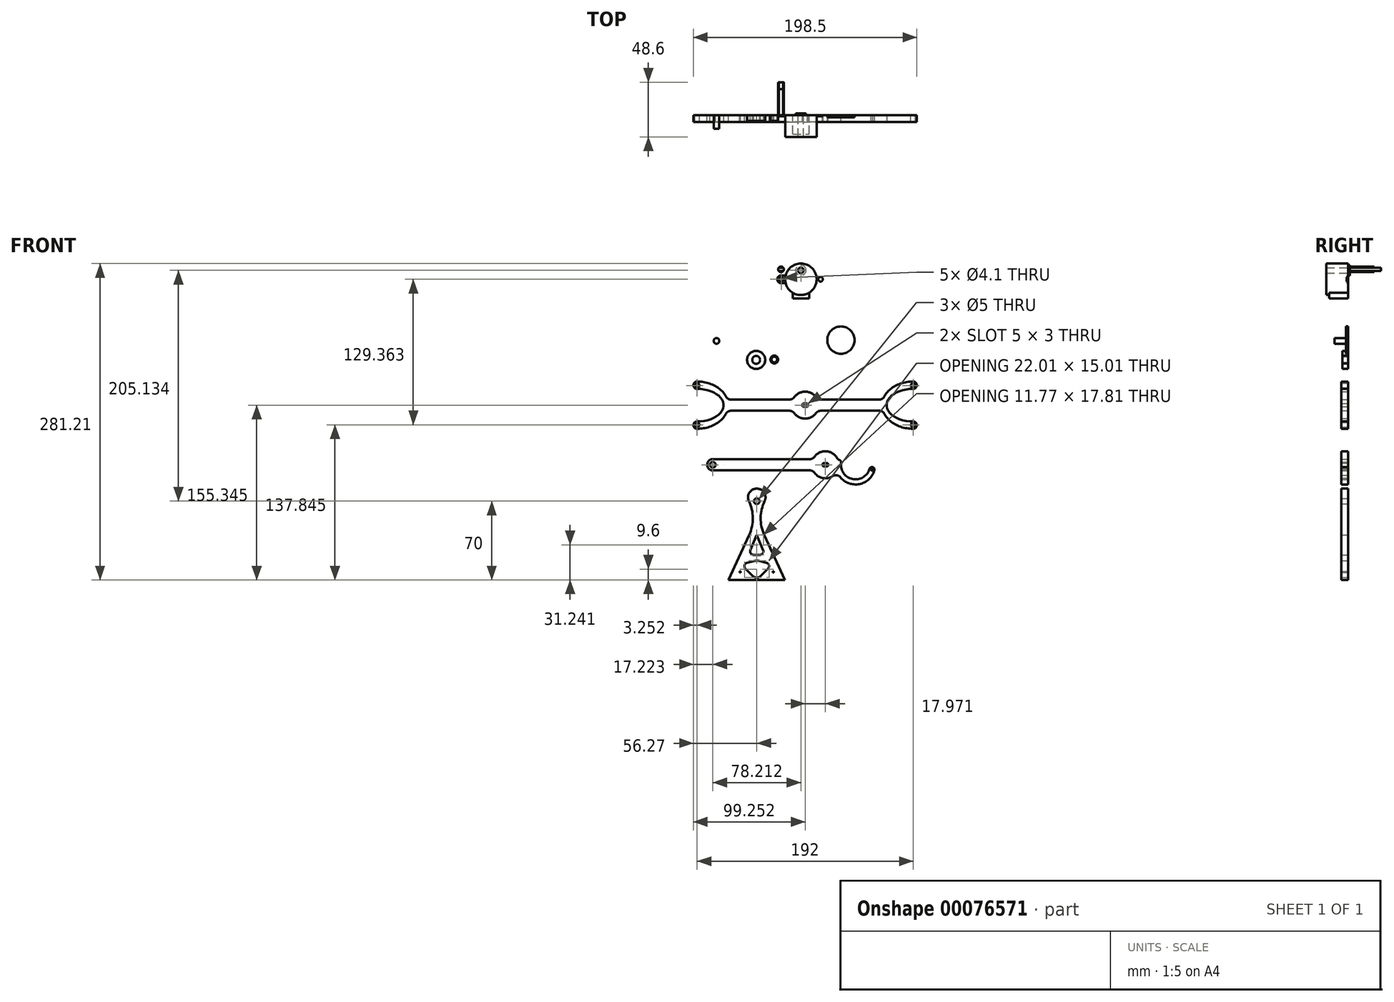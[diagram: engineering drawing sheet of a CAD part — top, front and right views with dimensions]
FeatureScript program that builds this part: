
annotation { "Feature Type Name" : "Feature", "Feature Type Description" : "" }
export const myFeature = defineFeature(function(context is Context, id is Id, definition is map)
    precondition{}
    {
        {
            var Q0;
            Q0=qCreatedBy(makeId("Front.planeOp"),FACE);
            var sketch = newSketch(context, id + "F0", { "sketchPlane" : qUnion([Q0])});
            skCircle(sketch, "E0", {"center": v(49.8, 38.16) * mm, "radius": 12.13 * mm});
            skSolve(sketch);
        }
        {
            var Q0;
            Q0=makeQuery(id+"F0.imprint","IMPRINT",FACE,{"disambiguationData":[TD([[makeQuery(id+"F0.imprint","IMPRINT",EDGE,{"derivedFrom":sQuery(id+"F0.wireOp",EDGE,"E0")}),1.0]])]});
            extrude(context, id + "F1", {"entities" : qUnion([Q0]), "depth" : 1.75 * mm});
        }
        {
            var Q0;
            Q0=qCreatedBy(makeId("Front.planeOp"),FACE);
            var sketch = newSketch(context, id + "F2", { "sketchPlane" : qUnion([Q0])});
            skLineSegment(sketch, "E1", {"start": v(-48, -14.65) * mm, "end": v(4.23, -14.65) * mm});
            skLineSegment(sketch, "E2", {"start": v(4.23, -24.65) * mm, "end": v(-48, -24.65) * mm});
            skArc(sketch, "E3", {"start": v(15.98, -18.15) * mm, "mid": v(15.48, -19.65) * mm, "end": v(15.98, -21.15) * mm});
            skArc(sketch, "E4", {"start": v(8.28, -26.71) * mm, "mid": v(12.54, -30.35) * mm, "end": v(17.98, -31.65) * mm});
            skArc(sketch, "E5.trimOffspring", {"start": v(17.98, -7.65) * mm, "mid": v(12.54, -8.96) * mm, "end": v(8.28, -12.6) * mm});
            skPoint(sketch, "E6.visualSharp", {"position": v(7.07, -14.65) * mm});
            skArc(sketch, "E6.filletArc", {"start": v(4.23, -14.65) * mm, "mid": v(6.5, -14.11) * mm, "end": v(8.28, -12.6) * mm});
            skPoint(sketch, "E7.visualSharp", {"position": v(7.07, -24.65) * mm});
            skArc(sketch, "E7.filletArc", {"start": v(8.28, -26.71) * mm, "mid": v(6.5, -25.2) * mm, "end": v(4.23, -24.65) * mm});
            skLineSegment(sketch, "E8.bottom", {"start": v(15.98, -21.15) * mm, "end": v(17.98, -21.15) * mm});
            skLineSegment(sketch, "E8.top", {"start": v(15.98, -18.15) * mm, "end": v(17.98, -18.15) * mm});
            skCircle(sketch, "E9", {"center": v(-78.02, -37.15) * mm, "radius": 2.05 * mm});
            skCircle(sketch, "E10", {"center": v(-78.02, -2.15) * mm, "radius": 2.05 * mm});
            skLineSegment(sketch, "E11", {"start": v(-78.02, -2.15) * mm, "end": v(-78.02, -37.15) * mm, "construction": true});
            skPoint(sketch, "E12", {"position": v(-78.02, -19.65) * mm});
            skEllipticalArc(sketch, "E13", {});
            skEllipticalArc(sketch, "E14", {});
            skPoint(sketch, "E15", {"position": v(-78.02, 1.35) * mm});
            skPoint(sketch, "E16", {"position": v(-78.02, -5.15) * mm});
            skPoint(sketch, "E17", {"position": v(-78.02, -40.65) * mm});
            skPoint(sketch, "E18", {"position": v(-78.02, -34.15) * mm});
            skArc(sketch, "E19", {"start": v(-78.02, 1.35) * mm, "mid": v(-81.27, -1.9) * mm, "end": v(-78.02, -5.15) * mm});
            skArc(sketch, "E20", {"start": v(-78.02, -34.15) * mm, "mid": v(-81.27, -37.4) * mm, "end": v(-78.02, -40.65) * mm});
            skEllipticalArc(sketch, "E21.trimOffspring", {});
            skPoint(sketch, "E22.visualSharp", {"position": v(-51.3, -14.65) * mm});
            skArc(sketch, "E22.filletArc", {"start": v(-52.44, -11.95) * mm, "mid": v(-50.6, -13.93) * mm, "end": v(-48, -14.65) * mm});
            skPoint(sketch, "E23.visualSharp", {"position": v(-51.3, -24.65) * mm});
            skArc(sketch, "E23.filletArc", {"start": v(-48, -24.65) * mm, "mid": v(-50.6, -25.38) * mm, "end": v(-52.44, -27.36) * mm});
            skLineSegment(sketch, "E24", {"start": v(17.98, -19.65) * mm, "end": v(17.98, 0) * mm});
            skLineSegment(sketch, "E25", {"start": v(17.98, -19.65) * mm, "end": v(17.98, -40.2) * mm});
            skPoint(sketch, "E25.endSnap0", {"position": v(17.98, -21.15) * mm});
            skArc(sketch, "E26.MirrorCS", {"start": v(27.69, -26.71) * mm, "mid": v(23.43, -30.35) * mm, "end": v(17.98, -31.65) * mm});
            skArc(sketch, "E27.MirrorCS", {"start": v(17.98, -7.65) * mm, "mid": v(23.43, -8.96) * mm, "end": v(27.69, -12.6) * mm});
            skArc(sketch, "E28.MirrorCS", {"start": v(31.73, -14.65) * mm, "mid": v(29.46, -14.11) * mm, "end": v(27.69, -12.6) * mm});
            skLineSegment(sketch, "E29.MirrorCS", {"start": v(19.98, -18.15) * mm, "end": v(17.98, -18.15) * mm});
            skArc(sketch, "E30.MirrorCS", {"start": v(19.98, -18.15) * mm, "mid": v(20.48, -19.65) * mm, "end": v(19.98, -21.15) * mm});
            skLineSegment(sketch, "E31.MirrorCS", {"start": v(19.98, -21.15) * mm, "end": v(17.98, -21.15) * mm});
            skArc(sketch, "E32.MirrorCS", {"start": v(27.69, -26.71) * mm, "mid": v(29.46, -25.2) * mm, "end": v(31.73, -24.65) * mm});
            skLineSegment(sketch, "E33.MirrorCS", {"start": v(83.96, -14.65) * mm, "end": v(31.73, -14.65) * mm});
            skLineSegment(sketch, "E34.MirrorCS", {"start": v(31.73, -24.65) * mm, "end": v(83.96, -24.65) * mm});
            skArc(sketch, "E35.MirrorCS", {"start": v(83.96, -24.65) * mm, "mid": v(86.56, -25.38) * mm, "end": v(88.4, -27.36) * mm});
            skArc(sketch, "E36.MirrorCS", {"start": v(88.4, -11.95) * mm, "mid": v(86.56, -13.93) * mm, "end": v(83.96, -14.65) * mm});
            skEllipticalArc(sketch, "E37.MirrorCS", {});
            skArc(sketch, "E38.MirrorCS", {"start": v(113.98, 1.35) * mm, "mid": v(117.23, -1.9) * mm, "end": v(113.98, -5.15) * mm});
            skCircle(sketch, "E39.MirrorC", {"center": v(113.98, -2.15) * mm, "radius": 2.05 * mm});
            skEllipticalArc(sketch, "E40.MirrorCS", {});
            skArc(sketch, "E41.MirrorCS", {"start": v(113.98, -34.15) * mm, "mid": v(117.23, -37.4) * mm, "end": v(113.98, -40.65) * mm});
            skCircle(sketch, "E42.MirrorC", {"center": v(113.98, -37.15) * mm, "radius": 2.05 * mm});
            skEllipticalArc(sketch, "E43.MirrorCS", {});
            const initialGuessF2  = {"E13": [-0.07801780587148666, -0.01965486932093423, 0, -1, 0.021, 0.0275, 6.283185307179586, 1.1950960830232749], "E14": [-0.07801780587148666, -0.01965486932093423, -1, 0, 0.0235, 0.0145, 1.5707963267948966, 4.71238898038469], "E21.trimOffspring": [-0.07801780587148666, -0.01965486932093423, 0, -1, 0.021, 0.0275, 1.9464965705665191, 3.141592653589793], "E37.MirrorCS": [0.11398219412851335, -0.01965486932093423, 0, -1, 0.021, 0.0275, 3.141592653589793, 4.336688736613067], "E40.MirrorCS": [0.11398219412851335, -0.01965486932093423, 1, 0, 0.0235, 0.0145, 1.5707963267948966, 4.71238898038469], "E43.MirrorCS": [0.11398219412851335, -0.01965486932093423, 0, -1, 0.021, 0.0275, 5.088089224156311, 6.283185307179586]};
            skSetInitialGuess(sketch, initialGuessF2);
            skSolve(sketch);
        }
        {
            var Q0;
            Q0 = qSketchRegion(id + "F2", true);
            extrude(context, id + "F3", {"entities" : qUnion([Q0]), "depth" : 6 * mm});
        }
        {
            var Q0;
            Q0=qCreatedBy(makeId("Front.planeOp"),FACE);
            var sketch = newSketch(context, id + "F4", { "sketchPlane" : qUnion([Q0])});
            skCircle(sketch, "E44", {"center": v(-60.76, 37.44) * mm, "radius": 2.5 * mm});
            skSolve(sketch);
        }
        {
            var Q0;
            Q0 = qSketchRegion(id + "F4", true);
            extrude(context, id + "F5", {"entities" : qUnion([Q0]), "depth" : 12 * mm});
        }
        {
            var Q0;
            Q0=qCreatedBy(makeId("Front.planeOp"),FACE);
            var sketch = newSketch(context, id + "F6", { "sketchPlane" : qUnion([Q0])});
            skCircle(sketch, "E45", {"center": v(-25.53, 20.6) * mm, "radius": 3.5 * mm});
            skCircle(sketch, "E46", {"center": v(-25.53, 20.6) * mm, "radius": 8 * mm});
            skSolve(sketch);
        }
        {
            var Q0;
            Q0=makeQuery(id+"F6.imprint","IMPRINT",FACE,{"disambiguationData":[TD([[makeQuery(id+"F6.imprint","IMPRINT",EDGE,{"derivedFrom":sQuery(id+"F6.wireOp",EDGE,"E45")}),-1.0]])]});
            extrude(context, id + "F7", {"entities" : qUnion([Q0]), "depth" : 5 * mm});
        }
        {
            var Q0;
            Q0=qCreatedBy(makeId("Front.planeOp"),FACE);
            var sketch = newSketch(context, id + "F8", { "sketchPlane" : qUnion([Q0])});
            skCircle(sketch, "E47", {"center": v(-9.4, 20.94) * mm, "radius": 3.5 * mm});
            skCircle(sketch, "E48", {"center": v(-9.4, 20.94) * mm, "radius": 2.5 * mm});
            skSolve(sketch);
        }
        {
            var Q0;
            Q0=makeQuery(id+"F8.imprint","IMPRINT",FACE,{"disambiguationData":[TD([[makeQuery(id+"F8.imprint","IMPRINT",EDGE,{"derivedFrom":sQuery(id+"F8.wireOp",EDGE,"E47")}),1.0]])]});
            extrude(context, id + "F9", {"entities" : qUnion([Q0]), "depth" : 5 * mm});
        }
        {
            var Q0;
            Q0=qCreatedBy(makeId("Front.planeOp"),FACE);
            var sketch = newSketch(context, id + "F10", { "sketchPlane" : qUnion([Q0])});
            skCircle(sketch, "E49", {"center": v(-25, -105) * mm, "radius": 2.5 * mm});
            skLineSegment(sketch, "E50", {"start": v(-50, -175) * mm, "end": v(0, -175) * mm});
            skLineSegment(sketch, "E51", {"start": v(-25, -175) * mm, "end": v(-25, -70.8) * mm, "construction": true});
            skLineSegment(sketch, "E52", {"start": v(-32, -105) * mm, "end": v(0, -175) * mm, "construction": true});
            skLineSegment(sketch, "E53", {"start": v(-18, -105) * mm, "end": v(-50, -175) * mm, "construction": true});
            skPoint(sketch, "E54.visualSharp", {"position": v(-50, -175) * mm});
            skPoint(sketch, "E55.visualSharp", {"position": v(0, -175) * mm});
            skLineSegment(sketch, "E56", {"start": v(-31.65, -134.85) * mm, "end": v(-50, -175) * mm});
            skLineSegment(sketch, "E57", {"start": v(0, -175) * mm, "end": v(-18.35, -134.85) * mm});
            skPoint(sketch, "E58.visualSharp", {"position": v(-25, -120.31) * mm});
            skArc(sketch, "E58.filletArc", {"start": v(-31.65, -134.85) * mm, "mid": v(-28.48, -119.89) * mm, "end": v(-32, -105) * mm});
            skArc(sketch, "E59.filletArc", {"start": v(-18, -105) * mm, "mid": v(-21.52, -119.89) * mm, "end": v(-18.35, -134.85) * mm});
            skPoint(sketch, "E60.visualSharp", {"position": v(-32, -105) * mm});
            skPoint(sketch, "E61.visualSharp", {"position": v(-18, -105) * mm});
            skLineSegment(sketch, "E62", {"start": v(-31.65, -134.85) * mm, "end": v(0, -175) * mm, "construction": true});
            skLineSegment(sketch, "E63", {"start": v(-18.35, -134.85) * mm, "end": v(-50, -175) * mm, "construction": true});
            skArc(sketch, "E64", {"start": v(-32, -105) * mm, "mid": v(-25, -93.81) * mm, "end": v(-18, -105) * mm});
            skLineSegment(sketch, "E65", {"start": v(-25, -143.28) * mm, "end": v(-35.5, -143.28) * mm, "construction": true});
            skLineSegment(sketch, "E66", {"start": v(-25, -143.28) * mm, "end": v(-14.5, -143.28) * mm, "construction": true});
            skLineSegment(sketch, "E67", {"start": v(-35.5, -143.28) * mm, "end": v(-25, -175) * mm, "construction": true});
            skLineSegment(sketch, "E68", {"start": v(-14.5, -143.28) * mm, "end": v(-25, -175) * mm, "construction": true});
            skPoint(sketch, "E69.second.point", {"position": v(-32.4, -152.67) * mm});
            skPoint(sketch, "E69.third.point", {"position": v(-17.6, -152.67) * mm});
            skLineSegment(sketch, "E70", {"start": v(-31.65, -134.85) * mm, "end": v(-18.35, -134.85) * mm, "construction": true});
            skLineSegment(sketch, "E71", {"start": v(-25, -134.85) * mm, "end": v(-30.67, -148.52) * mm});
            skLineSegment(sketch, "E72", {"start": v(-22.1, -152.67) * mm, "end": v(-27.9, -152.67) * mm});
            skLineSegment(sketch, "E73", {"start": v(-25, -134.85) * mm, "end": v(-19.33, -148.52) * mm});
            skArc(sketch, "E74.filletArc", {"start": v(-30.67, -148.52) * mm, "mid": v(-30.4, -151.33) * mm, "end": v(-27.9, -152.67) * mm});
            skArc(sketch, "E75.filletArc", {"start": v(-22.1, -152.67) * mm, "mid": v(-19.6, -151.33) * mm, "end": v(-19.33, -148.52) * mm});
            skLineSegment(sketch, "E76", {"start": v(-32.4, -152.67) * mm, "end": v(0, -175) * mm, "construction": true});
            skLineSegment(sketch, "E77", {"start": v(-17.6, -152.67) * mm, "end": v(-50, -175) * mm, "construction": true});
            skPoint(sketch, "E78.visualSharp", {"position": v(-25, -134.85) * mm});
            skLineSegment(sketch, "E79", {"start": v(-29.65, -160.97) * mm, "end": v(-20.35, -160.97) * mm, "construction": true});
            skLineSegment(sketch, "E80", {"start": v(-29.65, -160.97) * mm, "end": v(-38.94, -160.97) * mm, "construction": true});
            skLineSegment(sketch, "E81", {"start": v(-20.35, -160.97) * mm, "end": v(-11.06, -160.97) * mm, "construction": true});
            skPoint(sketch, "E82.visualSharp", {"position": v(-25, -157.76) * mm});
            skPoint(sketch, "E83.visualSharp", {"position": v(-38.94, -160.97) * mm});
            skPoint(sketch, "E84.visualSharp", {"position": v(-11.06, -160.97) * mm});
            skPoint(sketch, "E85.visualSharp", {"position": v(-25, -175) * mm});
            skPoint(sketch, "E86.visualSharp", {"position": v(-20.35, -160.97) * mm});
            skLineSegment(sketch, "E87", {"start": v(-35.14, -164.8) * mm, "end": v(-28.55, -171.43) * mm});
            skLineSegment(sketch, "E88", {"start": v(-14.86, -164.8) * mm, "end": v(-21.45, -171.43) * mm});
            skLineSegment(sketch, "E89", {"start": v(-26.12, -158.02) * mm, "end": v(-33.68, -159.76) * mm});
            skLineSegment(sketch, "E90", {"start": v(-23.88, -158.02) * mm, "end": v(-16.32, -159.76) * mm});
            skArc(sketch, "E91.filletArc", {"start": v(-23.88, -158.02) * mm, "mid": v(-25, -157.9) * mm, "end": v(-26.12, -158.02) * mm});
            skArc(sketch, "E92.filletArc", {"start": v(-33.68, -159.76) * mm, "mid": v(-35.89, -161.85) * mm, "end": v(-35.14, -164.8) * mm});
            skArc(sketch, "E93.filletArc", {"start": v(-14.86, -164.8) * mm, "mid": v(-14.11, -161.85) * mm, "end": v(-16.32, -159.76) * mm});
            skArc(sketch, "E94.filletArc", {"start": v(-28.55, -171.43) * mm, "mid": v(-25, -172.9) * mm, "end": v(-21.45, -171.43) * mm});
            skLineSegment(sketch, "E95", {"start": v(-25, -167.9) * mm, "end": v(-10.3, -167.9) * mm, "construction": true});
            skLineSegment(sketch, "E96", {"start": v(-25, -167.9) * mm, "end": v(-39.7, -167.9) * mm, "construction": true});
            skCircle(sketch, "E97", {"center": v(-39.7, -167.9) * mm, "radius": 0.5 * mm});
            skCircle(sketch, "E98", {"center": v(-10.3, -167.9) * mm, "radius": 0.5 * mm});
            skSolve(sketch);
        }
        {
            var Q0;
            Q0 = qSketchRegion(id + "F10", true);
            extrude(context, id + "F11", {"entities" : qUnion([Q0]), "depth" : 6 * mm});
        }
        {
            var Q0;
            Q0=qCreatedBy(makeId("Front.planeOp"),FACE);
            var sketch = newSketch(context, id + "F12", { "sketchPlane" : qUnion([Q0])});
            skArc(sketch, "E99", {"start": v(14.2, 106.2) * mm, "mid": v(5.6, 103.26) * mm, "end": v(0.64, 95.66) * mm});
            skLineSegment(sketch, "E100.right", {"start": v(-6.75, 92.2) * mm, "end": v(-6.75, 92.2) * mm});
            skPoint(sketch, "E101.visualSharp", {"position": v(-6.75, 95.66) * mm});
            skArc(sketch, "E101.filletArc", {"start": v(-3.3, 95.66) * mm, "mid": v(-5.74, 94.65) * mm, "end": v(-6.75, 92.2) * mm});
            skPoint(sketch, "E102.visualSharp", {"position": v(-6.75, 88.76) * mm});
            skArc(sketch, "E102.filletArc", {"start": v(-6.75, 92.2) * mm, "mid": v(-5.75, 89.79) * mm, "end": v(-3.35, 88.76) * mm});
            skLineSegment(sketch, "E103.MirrorCS", {"start": v(-3.3, 95.66) * mm, "end": v(0.64, 95.66) * mm});
            skLineSegment(sketch, "E104.MirrorCS", {"start": v(-3.35, 88.76) * mm, "end": v(0.64, 88.76) * mm});
            skLineSegment(sketch, "E105.MirrorCS", {"start": v(35.39, 91.8) * mm, "end": v(35.39, 91.8) * mm});
            skPoint(sketch, "E106.MirrorP", {"position": v(35.39, 95.25) * mm});
            skPoint(sketch, "E107.MirrorP", {"position": v(35.39, 88.35) * mm});
            skLineSegment(sketch, "E108", {"start": v(14.2, 92.2) * mm, "end": v(-3.3, 92.2) * mm, "construction": true});
            skCircle(sketch, "E109", {"center": v(-3.3, 92.2) * mm, "radius": 2.05 * mm});
            skLineSegment(sketch, "E110", {"start": v(14.2, 92.2) * mm, "end": v(14.2, 113.27) * mm, "construction": true});
            skLineSegment(sketch, "E111", {"start": v(14.2, 92.2) * mm, "end": v(14.2, 71.22) * mm, "construction": true});
            skPoint(sketch, "E100.left.end.orphan", {"position": v(35.15, 95.66) * mm});
            skPoint(sketch, "E112.orphan", {"position": v(35.15, 88.76) * mm});
            skArc(sketch, "E113.trimOffspring", {"start": v(14.2, 78.2) * mm, "mid": v(5.6, 81.16) * mm, "end": v(0.64, 88.76) * mm});
            skLineSegment(sketch, "E114.trimOffspring", {"start": v(0.64, 88.76) * mm, "end": v(-3.35, 88.76) * mm});
            skPoint(sketch, "E115.orphan", {"position": v(14.2, 106.2) * mm});
            skPoint(sketch, "E116.MirrorCS.end.orphan", {"position": v(14.2, 78.2) * mm});
            skArc(sketch, "E117", {"start": v(14.2, 104.8) * mm, "mid": v(9.6, 100.2) * mm, "end": v(14.2, 95.6) * mm});
            skLineSegment(sketch, "E118.trimOffspring", {"start": v(0.64, 95.66) * mm, "end": v(-3.3, 95.66) * mm});
            skArc(sketch, "E119.trimOffspring", {"start": v(0.64, 95.66) * mm, "mid": v(5.6, 103.26) * mm, "end": v(14.2, 106.2) * mm});
            skArc(sketch, "E120.trimOffspring", {"start": v(0.64, 88.76) * mm, "mid": v(5.6, 81.16) * mm, "end": v(14.2, 78.2) * mm});
            skLineSegment(sketch, "E121", {"start": v(6.85, 75.2) * mm, "end": v(14.2, 75.2) * mm});
            skLineSegment(sketch, "E122", {"start": v(6.85, 75.2) * mm, "end": v(6.85, 80.3) * mm});
            skLineSegment(sketch, "E123.MirrorCS", {"start": v(35.15, 92.2) * mm, "end": v(35.15, 92.2) * mm});
            skLineSegment(sketch, "E124.MirrorCS", {"start": v(27.77, 95.66) * mm, "end": v(31.7, 95.66) * mm});
            skLineSegment(sketch, "E125.MirrorCS", {"start": v(31.75, 88.76) * mm, "end": v(27.77, 88.76) * mm});
            skLineSegment(sketch, "E126.MirrorCS", {"start": v(14.2, 92.2) * mm, "end": v(31.7, 92.2) * mm, "construction": true});
            skCircle(sketch, "E127.MirrorC", {"center": v(31.7, 92.2) * mm, "radius": 2.05 * mm});
            skArc(sketch, "E128.MirrorCS", {"start": v(14.2, 104.8) * mm, "mid": v(18.8, 100.2) * mm, "end": v(14.2, 95.6) * mm});
            skLineSegment(sketch, "E129.MirrorCS", {"start": v(31.7, 95.66) * mm, "end": v(27.77, 95.66) * mm});
            skArc(sketch, "E130.MirrorCS", {"start": v(27.77, 95.66) * mm, "mid": v(22.8, 103.26) * mm, "end": v(14.2, 106.2) * mm});
            skArc(sketch, "E131.MirrorCS", {"start": v(27.77, 88.76) * mm, "mid": v(22.8, 81.16) * mm, "end": v(14.2, 78.2) * mm});
            skArc(sketch, "E132.MirrorCS", {"start": v(35.15, 92.2) * mm, "mid": v(34.16, 89.79) * mm, "end": v(31.75, 88.76) * mm});
            skArc(sketch, "E133.MirrorCS", {"start": v(14.2, 106.2) * mm, "mid": v(22.8, 103.26) * mm, "end": v(27.77, 95.66) * mm});
            skLineSegment(sketch, "E134.MirrorCS", {"start": v(27.77, 88.76) * mm, "end": v(31.75, 88.76) * mm});
            skArc(sketch, "E135.MirrorCS", {"start": v(31.7, 95.66) * mm, "mid": v(34.14, 94.65) * mm, "end": v(35.15, 92.2) * mm});
            skArc(sketch, "E136.MirrorCS", {"start": v(14.2, 78.2) * mm, "mid": v(22.8, 81.16) * mm, "end": v(27.77, 88.76) * mm});
            skLineSegment(sketch, "E137.MirrorCS", {"start": v(21.55, 75.2) * mm, "end": v(21.55, 80.3) * mm});
            skLineSegment(sketch, "E138.MirrorCS", {"start": v(21.55, 75.2) * mm, "end": v(14.2, 75.2) * mm});
            skArc(sketch, "E139", {"start": v(0.64, 88.76) * mm, "mid": v(0.2, 92.2) * mm, "end": v(0.64, 95.66) * mm});
            skArc(sketch, "E140", {"start": v(27.77, 88.76) * mm, "mid": v(28.2, 92.2) * mm, "end": v(27.77, 95.66) * mm});
            skCircle(sketch, "E141", {"center": v(14.17, 100.13) * mm, "radius": 2.5 * mm});
            skSolve(sketch);
        }
        {
            var Q0;
            Q0=makeQuery(id+"F12.imprint","IMPRINT",FACE,{"disambiguationData":[TD([[makeQuery(id+"F12.imprint","IMPRINT",EDGE,{"derivedFrom":sQuery(id+"F12.wireOp",EDGE,"E127.MirrorC")}),1.0]])]});
            var Q1;
            {var subQ2=sQuery(id+"F12.wireOp",EDGE,"E101.filletArc");Q1=makeQuery(id+"F12.imprint","IMPRINT",FACE,{"disambiguationData":[TD([[makeQuery(id+"F12.imprint","IMPRINT",EDGE,{"derivedFrom":subQ2}),1.0]])]});}
            extrude(context, id + "F13", {"entities" : qUnion([Q0, Q1]), "depth" : 1 * mm});
        }
        {
            var Q0;
            Q0=makeQuery(id+"F12.imprint","IMPRINT",FACE,{"disambiguationData":[TD([[makeQuery(id+"F12.imprint","IMPRINT",EDGE,{"derivedFrom":sQuery(id+"F12.wireOp",EDGE,"E117")}),-1.0]])]});
            var Q1;
            Q1=makeQuery(id+"F12.imprint","IMPRINT",FACE,{"disambiguationData":[TD([[makeQuery(id+"F12.imprint","IMPRINT",EDGE,{"derivedFrom":sQuery(id+"F12.wireOp",EDGE,"E117")}),1.0]])]});
            var Q2;
            {var subQ3=sQuery(id+"F12.wireOp",EDGE,"SmNPuWLQ-9DWJ-AX38-nrQ1-hNS1adnPU8HB.bottom");Q2=makeQuery(id+"F12.imprint","IMPRINT",FACE,{"disambiguationData":[TD([[makeQuery(id+"F12.imprint","IMPRINT",EDGE,{"derivedFrom":subQ3}),1.0]])]});}
            var Q3;
            {var subQ3=sQuery(id+"F12.wireOp",EDGE,"e798720e-68ba-4cf8-9b3b-daa968d9e4d6.trimOffspring");Q3=makeQuery(id+"F12.imprint","IMPRINT",FACE,{"disambiguationData":[TD([[makeQuery(id+"F12.imprint","IMPRINT",EDGE,{"derivedFrom":subQ3}),-1.0]])]});}
            var Q4;
            {var subQ4=sQuery(id+"F12.wireOp",EDGE,"SmNPuWLQ-9DWJ-AX38-nrQ1-hNS1adnPU8HB.bottom");Q4=makeQuery(id+"F12.imprint","IMPRINT",FACE,{"disambiguationData":[TD([[makeQuery(id+"F12.imprint","IMPRINT",EDGE,{"derivedFrom":subQ4}),-1.0]])]});}
            extrude(context, id + "F14", {"entities" : qUnion([Q0, Q1, Q2, Q3, Q4]), "depth" : 19.3 * mm});
        }
        {
            var Q0;
            Q0=makeQuery(id+"F12.imprint","IMPRINT",FACE,{"disambiguationData":[TD([[makeQuery(id+"F12.imprint","IMPRINT",EDGE,{"derivedFrom":sQuery(id+"F12.wireOp",EDGE,"E121")}),1.0]])]});
            extrude(context, id + "F15", {"entities" : qUnion([Q0]), "operationType" : NewBodyOperationType.ADD, "depth" : 16.8 * mm});
        }
        {
            var Q0;
            Q0=makeQuery(id+"F12.imprint","IMPRINT",FACE,{"disambiguationData":[TD([[makeQuery(id+"F12.imprint","IMPRINT",EDGE,{"derivedFrom":sQuery(id+"F12.wireOp",EDGE,"E117")}),1.0]])]});
            extrude(context, id + "F16", {"entities" : qUnion([Q0]), "operationType" : NewBodyOperationType.ADD, "oppositeDirection" : true, "depth" : 1.7 * mm});
        }
        {
            var Q0;
            Q0=qCreatedBy(makeId("Front.planeOp"),FACE);
            var sketch = newSketch(context, id + "F17", { "sketchPlane" : qUnion([Q0])});
            skArc(sketch, "E142", {"start": v(-3.46, 103.58) * mm, "mid": v(-5.96, 101.08) * mm, "end": v(-3.46, 98.58) * mm});
            skLineSegment(sketch, "E143.bottom", {"start": v(-3.46, 99.58) * mm, "end": v(-5.46, 99.58) * mm});
            skLineSegment(sketch, "E144.trimOffspring", {"start": v(-3.46, 102.58) * mm, "end": v(-5.46, 102.58) * mm});
            skPoint(sketch, "E143.left.end.orphan", {"position": v(0.04, 102.58) * mm});
            skPoint(sketch, "E145.orphan", {"position": v(0.04, 99.58) * mm});
            skPoint(sketch, "E143.right.start.orphan", {"position": v(-6.96, 99.58) * mm});
            skPoint(sketch, "E146.orphan", {"position": v(-6.96, 102.58) * mm});
            skArc(sketch, "E147.MirrorCS", {"start": v(-3.46, 103.58) * mm, "mid": v(-0.96, 101.08) * mm, "end": v(-3.46, 98.58) * mm});
            skLineSegment(sketch, "E148.MirrorCS", {"start": v(-3.46, 102.58) * mm, "end": v(-1.46, 102.58) * mm});
            skLineSegment(sketch, "E149.MirrorCS", {"start": v(-3.46, 99.58) * mm, "end": v(-1.46, 99.58) * mm});
            skSolve(sketch);
        }
        {
            var Q0;
            {var subQ3=sQuery(id+"F17.wireOp",EDGE,"E143.bottom");Q0=makeQuery(id+"F17.imprint","IMPRINT",FACE,{"disambiguationData":[TD([[makeQuery(id+"F17.imprint","IMPRINT",EDGE,{"derivedFrom":subQ3}),1.0]])]});}
            var Q1;
            {var subQ3=sQuery(id+"F17.wireOp",EDGE,"E144.trimOffspring");Q1=makeQuery(id+"F17.imprint","IMPRINT",FACE,{"disambiguationData":[TD([[makeQuery(id+"F17.imprint","IMPRINT",EDGE,{"derivedFrom":subQ3}),-1.0]])]});}
            extrude(context, id + "F18", {"entities" : qUnion([Q0, Q1]), "oppositeDirection" : true, "depth" : 23.3 * mm});
        }
        {
            var Q0;
            {var subQ4=sQuery(id+"F17.wireOp",EDGE,"E143.bottom");Q0=makeQuery(id+"F17.imprint","IMPRINT",FACE,{"disambiguationData":[TD([[makeQuery(id+"F17.imprint","IMPRINT",EDGE,{"derivedFrom":subQ4}),-1.0]])]});}
            extrude(context, id + "F19", {"entities" : qUnion([Q0]), "oppositeDirection" : true, "depth" : 29.3 * mm});
        }
        {
            var Q0;
            Q0=qCreatedBy(makeId("Front.planeOp"),FACE);
            var sketch = newSketch(context, id + "F20", { "sketchPlane" : qUnion([Q0])});
            skLineSegment(sketch, "E150", {"start": v(-64.05, -67.63) * mm, "end": v(22.2, -67.63) * mm});
            skLineSegment(sketch, "E151", {"start": v(22.2, -77.63) * mm, "end": v(-64.05, -77.63) * mm});
            skLineSegment(sketch, "E152", {"start": v(-69.05, -72.63) * mm, "end": v(-69.05, -72.63) * mm});
            skArc(sketch, "E153", {"start": v(49.16, -83.69) * mm, "mid": v(66.15, -89.8) * mm, "end": v(79.5, -77.63) * mm});
            skPoint(sketch, "E153.third.point", {"position": v(80.13, -70.83) * mm});
            skCircle(sketch, "E154", {"center": v(-64.05, -72.63) * mm, "radius": 2.5 * mm});
            skArc(sketch, "E155", {"start": v(33.95, -71.13) * mm, "mid": v(33.45, -72.63) * mm, "end": v(33.95, -74.13) * mm});
            skArc(sketch, "E156", {"start": v(49.88, -70.61) * mm, "mid": v(59.85, -85.31) * mm, "end": v(75.18, -76.35) * mm});
            skLineSegment(sketch, "E157", {"start": v(48.26, -68.32) * mm, "end": v(48.48, -68.39) * mm});
            skCircle(sketch, "E158", {"center": v(77.34, -77) * mm, "radius": 0.75 * mm});
            skArc(sketch, "E159", {"start": v(26.25, -79.7) * mm, "mid": v(33.8, -84.44) * mm, "end": v(42.54, -82.67) * mm});
            skPoint(sketch, "E160.start.orphan", {"position": v(45.95, -67.63) * mm});
            skPoint(sketch, "E161.orphan", {"position": v(45.95, -77.63) * mm});
            skArc(sketch, "E162.trimOffspring", {"start": v(46.49, -66.89) * mm, "mid": v(36.73, -60.66) * mm, "end": v(26.25, -65.58) * mm});
            skPoint(sketch, "E163.visualSharp", {"position": v(46.3, -78.7) * mm});
            skArc(sketch, "E163.filletArc", {"start": v(49.16, -83.69) * mm, "mid": v(46.04, -81.9) * mm, "end": v(42.54, -82.67) * mm});
            skPoint(sketch, "E164.visualSharp", {"position": v(47, -67.95) * mm});
            skArc(sketch, "E164.filletArc", {"start": v(46.49, -66.89) * mm, "mid": v(47.23, -67.78) * mm, "end": v(48.26, -68.32) * mm});
            skPoint(sketch, "E165.newPointA", {"position": v(79.5, -77.63) * mm});
            skArc(sketch, "E165.filletArc", {"start": v(49.88, -70.61) * mm, "mid": v(49.6, -69.24) * mm, "end": v(48.48, -68.39) * mm});
            skPoint(sketch, "E166.visualSharp", {"position": v(25.04, -67.63) * mm});
            skArc(sketch, "E166.filletArc", {"start": v(22.2, -67.63) * mm, "mid": v(24.47, -67.09) * mm, "end": v(26.25, -65.58) * mm});
            skPoint(sketch, "E167.visualSharp", {"position": v(25.04, -77.63) * mm});
            skArc(sketch, "E167.filletArc", {"start": v(26.25, -79.7) * mm, "mid": v(24.47, -78.18) * mm, "end": v(22.2, -77.63) * mm});
            skPoint(sketch, "E168.visualSharp", {"position": v(-69.05, -67.63) * mm});
            skArc(sketch, "E168.filletArc", {"start": v(-64.05, -67.63) * mm, "mid": v(-67.58, -69.1) * mm, "end": v(-69.05, -72.63) * mm});
            skPoint(sketch, "E169.visualSharp", {"position": v(-69.05, -77.63) * mm});
            skArc(sketch, "E169.filletArc", {"start": v(-69.05, -72.63) * mm, "mid": v(-67.58, -76.17) * mm, "end": v(-64.05, -77.63) * mm});
            skArc(sketch, "E170", {"start": v(75.18, -76.35) * mm, "mid": v(77.98, -74.84) * mm, "end": v(79.5, -77.63) * mm});
            skLineSegment(sketch, "E171.bottom", {"start": v(33.95, -74.13) * mm, "end": v(37.95, -74.13) * mm});
            skLineSegment(sketch, "E171.top", {"start": v(33.95, -71.13) * mm, "end": v(37.95, -71.13) * mm});
            skPoint(sketch, "E171.left.end.orphan", {"position": v(32.7, -71.13) * mm});
            skPoint(sketch, "E172.orphan", {"position": v(32.7, -74.13) * mm});
            skPoint(sketch, "E171.right.start.orphan", {"position": v(39.2, -74.13) * mm});
            skPoint(sketch, "E173.orphan", {"position": v(39.2, -71.13) * mm});
            skArc(sketch, "E174.trimOffspring", {"start": v(37.95, -74.13) * mm, "mid": v(38.45, -72.63) * mm, "end": v(37.95, -71.13) * mm});
            skSolve(sketch);
        }
        {
            var Q0;
            Q0 = qSketchRegion(id + "F20", true);
            extrude(context, id + "F21", {"entities" : qUnion([Q0]), "depth" : 6 * mm});
        }
    });
